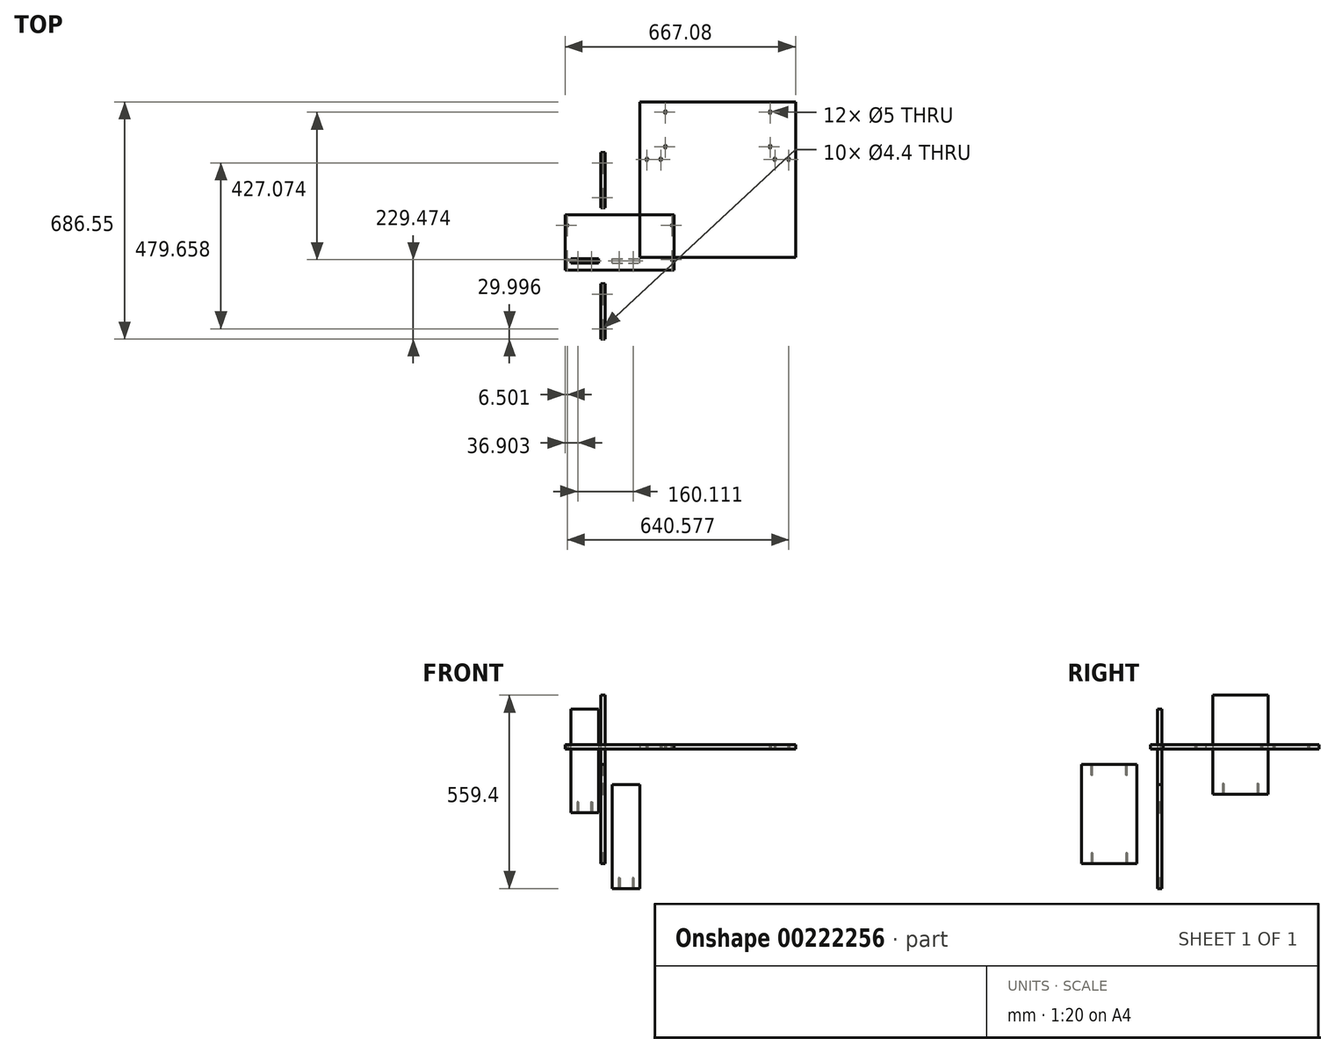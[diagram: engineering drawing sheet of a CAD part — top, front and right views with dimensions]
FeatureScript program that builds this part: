
annotation { "Feature Type Name" : "Feature", "Feature Type Description" : "" }
export const myFeature = defineFeature(function(context is Context, id is Id, definition is map)
    precondition{}
    {
        {
            var Q0;
            Q0=qCreatedBy(makeId("Top.planeOp"),FACE);
            var sketch = newSketch(context, id + "F0", { "sketchPlane" : qUnion([Q0])});
            skLineSegment(sketch, "E0", {"start": v(113.6, 3.66) * mm, "end": v(563.6, 3.66) * mm});
            skLineSegment(sketch, "E1", {"start": v(563.6, 3.66) * mm, "end": v(563.6, 453.66) * mm});
            skLineSegment(sketch, "E2", {"start": v(563.6, 453.66) * mm, "end": v(113.6, 453.66) * mm});
            skLineSegment(sketch, "E3", {"start": v(113.6, 453.66) * mm, "end": v(113.6, 3.66) * mm});
            skSolve(sketch);
        }
        {
            var Q0;
            Q0=qCreatedBy(makeId("Front.planeOp"),FACE);
            var sketch = newSketch(context, id + "F1", { "sketchPlane" : qUnion([Q0])});
            skLineSegment(sketch, "E4", {"start": v(-86.58, -184.12) * mm, "end": v(-86.58, 115.88) * mm});
            skLineSegment(sketch, "E5", {"start": v(-86.58, 115.88) * mm, "end": v(-6.58, 115.88) * mm});
            skLineSegment(sketch, "E6", {"start": v(-6.58, 115.88) * mm, "end": v(-6.58, -184.12) * mm});
            skLineSegment(sketch, "E7", {"start": v(-6.58, -184.12) * mm, "end": v(-86.58, -184.12) * mm});
            skSolve(sketch);
        }
        {
            var Q0;
            Q0=qCreatedBy(makeId("Front.planeOp"),FACE);
            var sketch = newSketch(context, id + "F2", { "sketchPlane" : qUnion([Q0])});
            skLineSegment(sketch, "E8", {"start": v(33.53, -403.35) * mm, "end": v(113.53, -403.35) * mm});
            skLineSegment(sketch, "E9", {"start": v(113.53, -403.35) * mm, "end": v(113.53, -103.35) * mm});
            skLineSegment(sketch, "E10", {"start": v(113.53, -103.35) * mm, "end": v(33.53, -103.35) * mm});
            skLineSegment(sketch, "E11", {"start": v(33.53, -103.35) * mm, "end": v(33.53, -403.35) * mm});
            skSolve(sketch);
        }
        {
            var Q0;
            Q0=qCreatedBy(makeId("Right.planeOp"),FACE);
            var sketch = newSketch(context, id + "F3", { "sketchPlane" : qUnion([Q0])});
            skLineSegment(sketch, "E12", {"start": v(-232.9, -331.3) * mm, "end": v(-232.9, -44.3) * mm});
            skLineSegment(sketch, "E13", {"start": v(-232.9, -44.3) * mm, "end": v(-72.9, -44.3) * mm});
            skLineSegment(sketch, "E14", {"start": v(-72.9, -44.3) * mm, "end": v(-72.9, -331.3) * mm});
            skLineSegment(sketch, "E15", {"start": v(-72.9, -331.3) * mm, "end": v(-232.9, -331.3) * mm});
            skSolve(sketch);
        }
        {
            var Q0;
            Q0=qCreatedBy(makeId("Right.planeOp"),FACE);
            var sketch = newSketch(context, id + "F4", { "sketchPlane" : qUnion([Q0])});
            skLineSegment(sketch, "E16", {"start": v(146.76, -130.95) * mm, "end": v(306.76, -130.95) * mm});
            skLineSegment(sketch, "E17", {"start": v(306.76, -130.95) * mm, "end": v(306.76, 156.05) * mm});
            skLineSegment(sketch, "E18", {"start": v(306.76, 156.05) * mm, "end": v(146.76, 156.05) * mm});
            skLineSegment(sketch, "E19", {"start": v(146.76, 156.05) * mm, "end": v(146.76, -130.95) * mm});
            skSolve(sketch);
        }
        {
            var Q0;
            Q0=qCreatedBy(makeId("Top.planeOp"),FACE);
            var sketch = newSketch(context, id + "F5", { "sketchPlane" : qUnion([Q0])});
            skLineSegment(sketch, "E20", {"start": v(-103.48, 126.58) * mm, "end": v(-103.48, -33.42) * mm});
            skLineSegment(sketch, "E21", {"start": v(-103.48, -33.42) * mm, "end": v(212.52, -33.42) * mm});
            skLineSegment(sketch, "E22", {"start": v(212.52, -33.42) * mm, "end": v(212.52, 126.58) * mm});
            skLineSegment(sketch, "E23", {"start": v(212.52, 126.58) * mm, "end": v(-103.48, 126.58) * mm});
            skPoint(sketch, "E24", {"position": v(-96.98, -3.42) * mm});
            skPoint(sketch, "E25", {"position": v(-96.98, 96.58) * mm});
            skPoint(sketch, "E26", {"position": v(206.02, -3.42) * mm});
            skPoint(sketch, "E27", {"position": v(206.02, 96.58) * mm});
            skSolve(sketch);
        }
        {
            var Q0;
            Q0 = qSketchRegion(id + "F0", true);
            extrude(context, id + "F6", {"entities" : qUnion([Q0]), "depth" : 13 * mm});
        }
        {
            var Q0;
            Q0 = qSketchRegion(id + "F1", true);
            extrude(context, id + "F7", {"entities" : qUnion([Q0]), "depth" : 13 * mm});
        }
        {
            var Q0;
            Q0=makeQuery(id+"F2.imprint","IMPRINT",FACE,{"disambiguationData":[TD([[makeQuery(id+"F2.imprint","IMPRINT",EDGE,{"derivedFrom":sQuery(id+"F2.wireOp",EDGE,"E8")}),1.0]])]});
            extrude(context, id + "F8", {"entities" : qUnion([Q0]), "depth" : 13 * mm});
        }
        {
            var Q0;
            Q0 = qSketchRegion(id + "F3", true);
            extrude(context, id + "F9", {"entities" : qUnion([Q0]), "depth" : 13 * mm});
        }
        {
            var Q0;
            Q0=makeQuery(id+"F4.imprint","IMPRINT",FACE,{"disambiguationData":[TD([[makeQuery(id+"F4.imprint","IMPRINT",EDGE,{"derivedFrom":sQuery(id+"F4.wireOp",EDGE,"E16")}),1.0]])]});
            extrude(context, id + "F10", {"entities" : qUnion([Q0]), "depth" : 13 * mm});
        }
        {
            var Q0;
            Q0=makeQuery(id+"F5.imprint","IMPRINT",FACE,{"disambiguationData":[TD([[makeQuery(id+"F5.imprint","IMPRINT",EDGE,{"derivedFrom":sQuery(id+"F5.wireOp",EDGE,"E20")}),1.0]])]});
            extrude(context, id + "F11", {"entities" : qUnion([Q0]), "depth" : 13 * mm});
        }
        {
            var Q0;
            Q0=makeQuery(id+"F6.opExtrude","CAP_FACE",FACE,{"disambiguationData":[OSD([sQuery(id+"F0.wireOp",EDGE,"E0"),sQuery(id+"F0.wireOp",EDGE,"E1"),sQuery(id+"F0.wireOp",EDGE,"E2"),sQuery(id+"F0.wireOp",EDGE,"E3")])],"isStart":true});
            var sketch = newSketch(context, id + "F12", { "sketchPlane" : qUnion([Q0])});
            skPoint(sketch, "E28", {"position": v(133.6, -287.16) * mm});
            skPoint(sketch, "E29", {"position": v(173.6, -287.16) * mm});
            skPoint(sketch, "E30", {"position": v(503.6, -287.16) * mm});
            skPoint(sketch, "E31", {"position": v(543.6, -287.16) * mm});
            skPoint(sketch, "E32", {"position": v(187.1, -323.66) * mm});
            skPoint(sketch, "E33", {"position": v(187.1, -423.66) * mm});
            skPoint(sketch, "E34", {"position": v(490.1, -323.66) * mm});
            skPoint(sketch, "E35", {"position": v(490.1, -423.66) * mm});
            skSolve(sketch);
        }
        {
            var Q0;
            Q0=makeQuery(id+"F7.opExtrude","SWEPT_FACE",FACE,{"disambiguationData":[OSD([sQuery(id+"F1.wireOp",EDGE,"E7")])]});
            var sketch = newSketch(context, id + "F13", { "sketchPlane" : qUnion([Q0])});
            skPoint(sketch, "E36", {"position": v(-66.58, 6.5) * mm});
            skPoint(sketch, "E36.positionSnap0", {"position": v(-86.58, 6.5) * mm});
            skPoint(sketch, "E37", {"position": v(-26.58, 6.5) * mm});
            skPoint(sketch, "E37.positionSnap0", {"position": v(-6.58, 6.5) * mm});
            skSolve(sketch);
        }
        {
            var Q0;
            Q0=makeQuery(id+"F8.opExtrude","SWEPT_FACE",FACE,{"disambiguationData":[OSD([sQuery(id+"F2.wireOp",EDGE,"E8")])]});
            var sketch = newSketch(context, id + "F14", { "sketchPlane" : qUnion([Q0])});
            skPoint(sketch, "E38", {"position": v(53.53, 6.5) * mm});
            skPoint(sketch, "E38.positionSnap0", {"position": v(33.53, 6.5) * mm});
            skPoint(sketch, "E39", {"position": v(93.53, 6.5) * mm});
            skSolve(sketch);
        }
        {
            var Q0;
            Q0=makeQuery(id+"F9.opExtrude","SWEPT_FACE",FACE,{"disambiguationData":[OSD([sQuery(id+"F3.wireOp",EDGE,"E15")])]});
            var sketch = newSketch(context, id + "F15", { "sketchPlane" : qUnion([Q0])});
            skPoint(sketch, "E40", {"position": v(6.5, 202.9) * mm});
            skPoint(sketch, "E40.positionSnap0", {"position": v(6.5, 232.9) * mm});
            skPoint(sketch, "E41", {"position": v(6.5, 102.9) * mm});
            skSolve(sketch);
        }
        {
            var Q0;
            Q0=makeQuery(id+"F10.opExtrude","SWEPT_FACE",FACE,{"disambiguationData":[OSD([sQuery(id+"F4.wireOp",EDGE,"E16")])]});
            var sketch = newSketch(context, id + "F16", { "sketchPlane" : qUnion([Q0])});
            skPoint(sketch, "E42", {"position": v(6.5, -176.76) * mm});
            skPoint(sketch, "E42.positionSnap0", {"position": v(6.5, -146.76) * mm});
            skPoint(sketch, "E43", {"position": v(6.5, -276.76) * mm});
            skSolve(sketch);
        }
        {
            var Q0;
            Q0=sQuery(id+"F12.wireOp",VERTEX,"E33");
            var Q1;
            Q1=sQuery(id+"F12.wireOp",VERTEX,"E32");
            var Q2;
            Q2=sQuery(id+"F12.wireOp",VERTEX,"E29");
            var Q3;
            Q3=sQuery(id+"F12.wireOp",VERTEX,"E28");
            var Q4;
            Q4=sQuery(id+"F12.wireOp",VERTEX,"E35");
            var Q5;
            Q5=sQuery(id+"F12.wireOp",VERTEX,"E34");
            var Q6;
            Q6=sQuery(id+"F12.wireOp",VERTEX,"E30");
            var Q7;
            Q7=sQuery(id+"F12.wireOp",VERTEX,"E31");
            var Q8;
            Q8=makeQuery(id+"F6.opExtrude","SWEPT_BODY",BODY,{"disambiguationData":[OSD([sQuery(id+"F0.wireOp",EDGE,"E0"),sQuery(id+"F0.wireOp",EDGE,"E1"),sQuery(id+"F0.wireOp",EDGE,"E2"),sQuery(id+"F0.wireOp",EDGE,"E3")])]});
            hole(context, id + "F17", {"style" : HoleStyle.C_SINK, "endStyle" : HoleEndStyle.THROUGH, "standardTappedOrClearance" : lookupTablePath({ "standard" : "ISO", "size" : "5", "type" : "Drilled" }), "standardBlindInLast" : lookupTablePath({ "standard" : "ISO", "size" : "5", "type" : "Drilled" }), "holeDiameter" : 5 * mm, "cSinkDiameter" : 11.2 * mm, "cSinkAngle" : 90 * degree, "locations" : qUnion([Q0, Q1, Q2, Q3, Q4, Q5, Q6, Q7]), "scope" : qUnion([Q8]), "isTappedThrough" : true});
        }
        {
            var Q0;
            Q0=sQuery(id+"F13.wireOp",VERTEX,"E36");
            var Q1;
            Q1=sQuery(id+"F13.wireOp",VERTEX,"E37");
            var Q2;
            Q2=makeQuery(id+"F7.opExtrude","SWEPT_BODY",BODY,{"disambiguationData":[OSD([sQuery(id+"F1.wireOp",EDGE,"E4"),sQuery(id+"F1.wireOp",EDGE,"E5"),sQuery(id+"F1.wireOp",EDGE,"E6"),sQuery(id+"F1.wireOp",EDGE,"E7")])]});
            hole(context, id + "F18", {"style" : HoleStyle.SIMPLE, "endStyle" : HoleEndStyle.BLIND, "standardTappedOrClearance" : lookupTablePath({ "standard" : "ISO", "engagement" : "25%", "pitch" : "0.9 mm", "size" : "M5", "type" : "Tapped" }), "standardBlindInLast" : lookupTablePath({ "standard" : "ISO", "engagement" : "25%", "pitch" : "0.9 mm", "size" : "M5", "type" : "Tapped" }), "holeDiameter" : 4.4 * mm, "holeDepth" : 30 * mm, "locations" : qUnion([Q0, Q1]), "scope" : qUnion([Q2])});
        }
        {
            var Q0;
            Q0=sQuery(id+"F14.wireOp",VERTEX,"E38");
            var Q1;
            Q1=sQuery(id+"F14.wireOp",VERTEX,"E39");
            var Q2;
            Q2=makeQuery(id+"F8.opExtrude","SWEPT_BODY",BODY,{"disambiguationData":[OSD([sQuery(id+"F2.wireOp",EDGE,"E8"),sQuery(id+"F2.wireOp",EDGE,"E9"),sQuery(id+"F2.wireOp",EDGE,"E10"),sQuery(id+"F2.wireOp",EDGE,"E11")])]});
            hole(context, id + "F19", {"style" : HoleStyle.SIMPLE, "endStyle" : HoleEndStyle.BLIND, "standardTappedOrClearance" : lookupTablePath({ "standard" : "ISO", "engagement" : "25%", "pitch" : "0.9 mm", "size" : "M5", "type" : "Tapped" }), "standardBlindInLast" : lookupTablePath({ "standard" : "ISO", "engagement" : "25%", "pitch" : "0.9 mm", "size" : "M5", "type" : "Tapped" }), "holeDiameter" : 4.4 * mm, "holeDepth" : 30 * mm, "locations" : qUnion([Q0, Q1]), "scope" : qUnion([Q2])});
        }
        {
            var Q0;
            Q0=sQuery(id+"F15.wireOp",VERTEX,"E40");
            var Q1;
            Q1=sQuery(id+"F15.wireOp",VERTEX,"E41");
            var Q2;
            Q2=makeQuery(id+"F9.opExtrude","SWEPT_BODY",BODY,{"disambiguationData":[OSD([sQuery(id+"F3.wireOp",EDGE,"E12"),sQuery(id+"F3.wireOp",EDGE,"E13"),sQuery(id+"F3.wireOp",EDGE,"E14"),sQuery(id+"F3.wireOp",EDGE,"E15")])]});
            hole(context, id + "F20", {"style" : HoleStyle.SIMPLE, "endStyle" : HoleEndStyle.BLIND, "standardTappedOrClearance" : lookupTablePath({ "standard" : "ISO", "engagement" : "25%", "pitch" : "0.9 mm", "size" : "M5", "type" : "Tapped" }), "standardBlindInLast" : lookupTablePath({ "standard" : "ISO", "engagement" : "25%", "pitch" : "0.9 mm", "size" : "M5", "type" : "Tapped" }), "holeDiameter" : 4.4 * mm, "holeDepth" : 30 * mm, "locations" : qUnion([Q0, Q1]), "scope" : qUnion([Q2])});
        }
        {
            var Q0;
            Q0=sQuery(id+"F16.wireOp",VERTEX,"E42");
            var Q1;
            Q1=sQuery(id+"F16.wireOp",VERTEX,"E43");
            var Q2;
            Q2=makeQuery(id+"F10.opExtrude","SWEPT_BODY",BODY,{"disambiguationData":[OSD([sQuery(id+"F4.wireOp",EDGE,"E16"),sQuery(id+"F4.wireOp",EDGE,"E17"),sQuery(id+"F4.wireOp",EDGE,"E18"),sQuery(id+"F4.wireOp",EDGE,"E19")])]});
            hole(context, id + "F21", {"style" : HoleStyle.SIMPLE, "endStyle" : HoleEndStyle.BLIND, "standardTappedOrClearance" : lookupTablePath({ "standard" : "ISO", "engagement" : "25%", "pitch" : "0.9 mm", "size" : "M5", "type" : "Tapped" }), "standardBlindInLast" : lookupTablePath({ "standard" : "ISO", "engagement" : "25%", "pitch" : "0.9 mm", "size" : "M5", "type" : "Tapped" }), "holeDiameter" : 4.4 * mm, "holeDepth" : 30 * mm, "locations" : qUnion([Q0, Q1]), "scope" : qUnion([Q2])});
        }
        {
            var Q0;
            Q0=makeQuery(id+"F9.opExtrude","SWEPT_FACE",FACE,{"disambiguationData":[OSD([sQuery(id+"F3.wireOp",EDGE,"E13")])]});
            var sketch = newSketch(context, id + "F22", { "sketchPlane" : qUnion([Q0])});
            skPoint(sketch, "E44", {"position": v(6.5, -202.9) * mm});
            skPoint(sketch, "E44.positionSnap0", {"position": v(6.5, -232.9) * mm});
            skPoint(sketch, "E45", {"position": v(6.5, -102.9) * mm});
            skPoint(sketch, "E45.positionSnap0", {"position": v(6.5, -72.9) * mm});
            skSolve(sketch);
        }
        {
            var Q0;
            Q0=sQuery(id+"F22.wireOp",VERTEX,"E45");
            var Q1;
            Q1=sQuery(id+"F22.wireOp",VERTEX,"E44");
            var Q2;
            Q2=makeQuery(id+"F9.opExtrude","SWEPT_BODY",BODY,{"disambiguationData":[OSD([sQuery(id+"F3.wireOp",EDGE,"E12"),sQuery(id+"F3.wireOp",EDGE,"E13"),sQuery(id+"F3.wireOp",EDGE,"E14"),sQuery(id+"F3.wireOp",EDGE,"E15")])]});
            hole(context, id + "F23", {"style" : HoleStyle.SIMPLE, "endStyle" : HoleEndStyle.BLIND, "standardTappedOrClearance" : lookupTablePath({ "standard" : "ISO", "engagement" : "25%", "pitch" : "0.9 mm", "size" : "M5", "type" : "Tapped" }), "standardBlindInLast" : lookupTablePath({ "standard" : "ISO", "engagement" : "25%", "pitch" : "0.9 mm", "size" : "M5", "type" : "Tapped" }), "holeDiameter" : 4.4 * mm, "holeDepth" : 30 * mm, "locations" : qUnion([Q0, Q1]), "scope" : qUnion([Q2])});
        }
        {
            var Q0;
            Q0=sQuery(id+"F5.wireOp",VERTEX,"E24");
            var Q1;
            Q1=sQuery(id+"F5.wireOp",VERTEX,"E25");
            var Q2;
            Q2=sQuery(id+"F5.wireOp",VERTEX,"E27");
            var Q3;
            Q3=sQuery(id+"F5.wireOp",VERTEX,"E26");
            var Q4;
            Q4=makeQuery(id+"F11.opExtrude","SWEPT_BODY",BODY,{"disambiguationData":[OSD([sQuery(id+"F5.wireOp",EDGE,"E20"),sQuery(id+"F5.wireOp",EDGE,"E21"),sQuery(id+"F5.wireOp",EDGE,"E22"),sQuery(id+"F5.wireOp",EDGE,"E23")])]});
            hole(context, id + "F24", {"style" : HoleStyle.SIMPLE, "endStyle" : HoleEndStyle.THROUGH, "oppositeDirection" : true, "standardTappedOrClearance" : lookupTablePath({ "standard" : "ISO", "size" : "5", "type" : "Drilled" }), "standardBlindInLast" : lookupTablePath({ "standard" : "ISO", "size" : "5", "type" : "Drilled" }), "holeDiameter" : 5 * mm, "locations" : qUnion([Q0, Q1, Q2, Q3]), "scope" : qUnion([Q4]), "isTappedThrough" : true});
        }
    });
